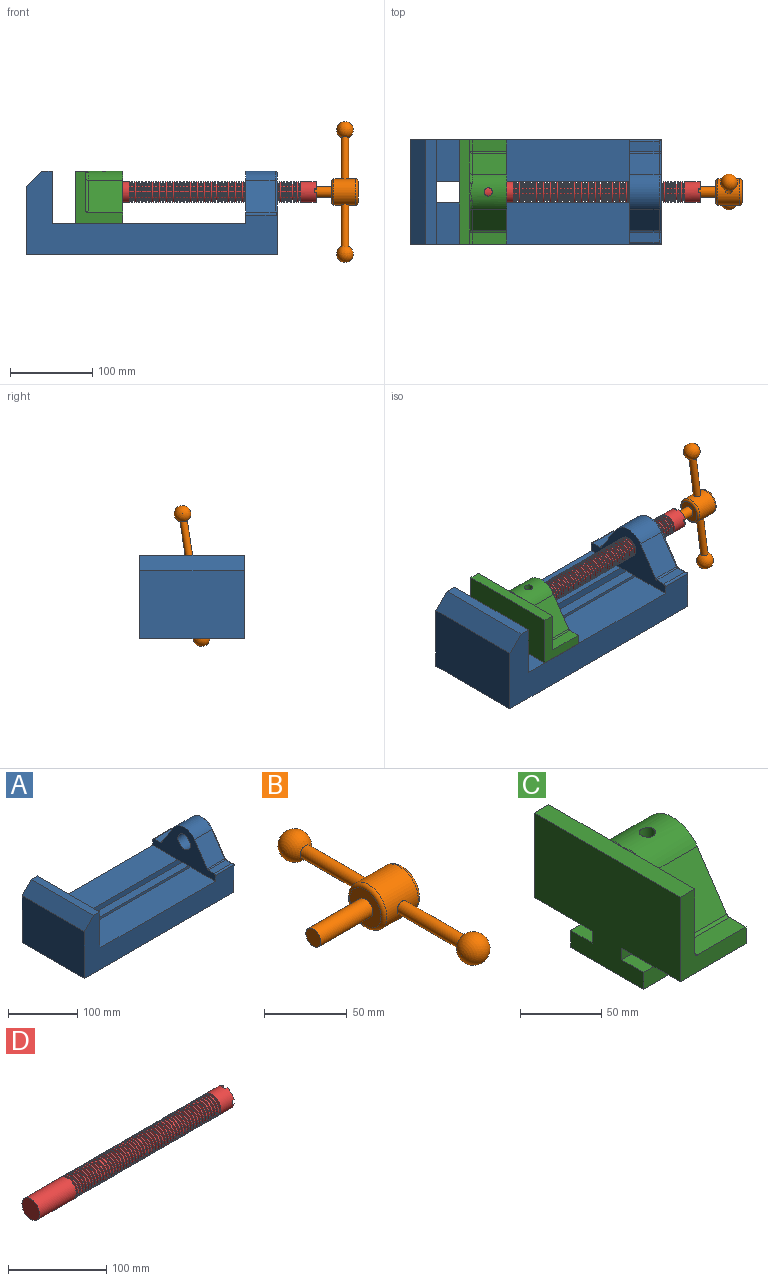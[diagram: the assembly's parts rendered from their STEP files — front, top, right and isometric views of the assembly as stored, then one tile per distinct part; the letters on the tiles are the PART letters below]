
ASSEMBLY  parts=4 mates=4
PART A: 39 faces, bbox 304.8x127x103.7 mm
  f0: plane 234.95x50.8mm, normal (0,0,1), area 11935.5mm2, adj f2,f8,f16,f26
  f1: plane 234.95x50.8mm, normal (0,0,1), area 11935.5mm2, adj f2,f9,f16,f27
  f2: plane 127x101.6mm, normal (1,0,0), area 9516.1mm2, adj f0,f1,f3,f6,f8,f9,f18,f19
  f3: plane 127x12.7mm, normal (0,0,1), area 1612.9mm2, adj f2,f4,f8,f9
  f4: plane 127x19.05mm, normal (-0.71,0,0.71), area 3421.5mm2, adj f3,f5,f8,f9
  f5: plane 127x82.55mm, normal (-1,0,0), area 10483.9mm2, adj f4,f6,f8,f9
  f6: plane 304.8x127mm, normal (0,0,-1), area 31774.1mm2, adj f2,f5,f7,f8,f9,f21,f22
  f7: plane 127x99.06mm, normal (1,0,0), area 7097.5mm2, adj f6,f8,f9,f14,f17,f18,f19,f20
  f8: plane 304.8x101.6mm, normal (0,-1,0), area 13834.6mm2, adj f0,f2,f3,f4,f5,f6,f7,f16
  f9: plane 304.8x101.6mm, normal (0,1,0), area 13834.6mm2, adj f1,f2,f3,f4,f5,f6,f7,f16
  f10: plane 35.56x11.98mm, normal (0,0,1), area 426mm2, adj f16,f28,f29,f30
  f11: plane 38.43x35.56mm, normal (0,0.83,0.56), area 1645.4mm2, adj f12,f16,f29,f32
  f12: cylinder r=25.4mm len=42.19mm, axis (1,0,0), area 1770.2mm2, adj f11,f13,f16,f33
  f13: plane 38.43x35.56mm, normal (0,-0.83,0.56), area 1645.4mm2, adj f12,f16,f34,f35
  f14: cylinder r=12.7mm len=38.1mm, axis (1,0,0), area 3040.2mm2, adj f7,f16
  f15: plane 35.56x11.98mm, normal (0,0,1), area 426mm2, adj f16,f34,f36,f38
  f16: plane 127x63.5mm, normal (-1,0,0), area 4155.5mm2, adj f0,f1,f8,f9,f10,f11,f12,f13
  f17: plane 38.1x25.4mm, normal (0,0,-1), area 967.7mm2, adj f7,f16,f26,f27
  f18: plane 273.05x19.05mm, normal (0,0,-1), area 5201.6mm2, adj f2,f7,f19,f26
  f19: plane 273.05x12.7mm, normal (0,1,0), area 3467.7mm2, adj f2,f7,f18,f20
  f20: plane 273.05x19.05mm, normal (0,0,1), area 5201.6mm2, adj f2,f7,f19,f21
  f21: plane 273.05x16.51mm, normal (0,1,0), area 4508.1mm2, adj f2,f6,f7,f20
  f22: plane 273.05x16.51mm, normal (0,-1,0), area 4508.1mm2, adj f2,f6,f7,f23
  f23: plane 273.05x19.05mm, normal (0,0,1), area 5201.6mm2, adj f2,f7,f22,f24
  f24: plane 273.05x12.7mm, normal (0,-1,0), area 3467.7mm2, adj f2,f7,f23,f25
  f25: plane 273.05x19.05mm, normal (0,0,-1), area 5201.6mm2, adj f2,f7,f24,f27
  f26: plane 273.05x8.89mm, normal (0,1,0), area 2427.4mm2, adj f0,f2,f7,f17,f18
  f27: plane 273.05x8.89mm, normal (0,-1,0), area 2427.4mm2, adj f1,f2,f7,f17,f25
  f28: cylinder r=2.54mm len=38.1mm, axis (1,0,0), area 148.3mm2, adj f9,f10,f16,f30
  f29: cylinder r=2.54mm len=35.56mm, axis (-1,0,0), area 88.5mm2, adj f10,f11,f16,f31
  f30: cylinder r=2.54mm len=14.52mm, axis (0,1,0), area 54.3mm2, adj f7,f10,f28,f31
  f31: torus R=5.08mm, axis (-1,0,0), area 13.5mm2, adj f7,f29,f30,f32
  f32: cylinder r=2.54mm len=39.84mm, axis (0,0.56,-0.83), area 184.6mm2, adj f7,f11,f31,f33
  f33: torus R=22.86mm, axis (-1,0,0), area 191.4mm2, adj f7,f12,f32,f35
  f34: cylinder r=2.54mm len=35.56mm, axis (-1,0,0), area 88.5mm2, adj f13,f15,f16,f37
  f35: cylinder r=2.54mm len=39.84mm, axis (0,0.56,0.83), area 184.6mm2, adj f7,f13,f33,f37
  f36: cylinder r=2.54mm len=38.1mm, axis (-1,0,0), area 148.3mm2, adj f8,f15,f16,f38
  f37: torus R=5.08mm, axis (-1,0,0), area 13.5mm2, adj f7,f34,f35,f38
  f38: cylinder r=2.54mm len=14.52mm, axis (0,1,0), area 54.3mm2, adj f7,f15,f36,f37
PART B: 11 faces, bbox 76.2x172.7x34.4 mm
  f0: sphere r=10.16mm, area 1231.8mm2, adj f1
  f1: cylinder r=4.45mm len=51.82mm, axis (0,1,0), area 1438.5mm2, adj f0,f4
  f2: sphere r=10.16mm, area 1231.8mm2, adj f3
  f3: cylinder r=4.45mm len=51.82mm, axis (0,1,0), area 1438.5mm2, adj f2,f4
  f4: cylinder r=15.88mm len=31.75mm, axis (-1,0,0), area 2534.7mm2, adj f1,f3,f9,f10
  f5: cylinder r=6.35mm len=44.45mm, axis (-1,0,0), area 1773.5mm2, adj f6,f8
  f6: plane 12.7x12.7mm, normal (-1,0,0), area 126.7mm2, adj f5
  f7: plane 26.67x26.67mm, normal (1,0,0), area 558.6mm2, adj f10
  f8: plane 26.67x26.67mm, normal (-1,0,0), area 432mm2, adj f5,f9
  f9: torus R=13.33mm, axis (1,0,0), area 374.8mm2, adj f4,f8
  f10: torus R=13.33mm, axis (1,0,0), area 374.8mm2, adj f4,f7
PART C: 36 faces, bbox 57.2x127x89 mm
  f0: plane 57.15x50.8mm, normal (0,0,-1), area 2903.2mm2, adj f6,f9,f10,f23
  f1: cylinder r=12.7mm len=44.45mm, axis (1,0,0), area 3464.3mm2, adj f6,f15,f16
  f2: plane 41.91x14.52mm, normal (0,0,1), area 608.5mm2, adj f6,f11,f24,f25
  f3: plane 51.86x48.26mm, normal (1,0,0), area 1495.7mm2, adj f8,f10,f31,f33,f35
  f4: plane 51.86x48.26mm, normal (1,0,0), area 1495.7mm2, adj f8,f11,f24,f28,f29
  f5: plane 57.15x50.8mm, normal (0,0,-1), area 2903.2mm2, adj f6,f9,f11,f22
  f6: plane 127x85.09mm, normal (1,0,0), area 5190.6mm2, adj f0,f1,f2,f5,f7,f10,f11,f12
  f7: plane 41.91x14.52mm, normal (0,0,1), area 608.5mm2, adj f6,f10,f30,f31
  f8: plane 127x12.7mm, normal (0,0,1), area 1612.9mm2, adj f3,f4,f9,f10,f11,f26,f34
  f9: plane 127x85.09mm, normal (-1,0,0), area 9096.8mm2, adj f0,f5,f8,f10,f11,f17,f18,f19
  f10: plane 63.5x57.15mm, normal (0,-1,0), area 1372.3mm2, adj f0,f3,f6,f7,f8,f9,f31
  f11: plane 63.5x57.15mm, normal (0,1,0), area 1372.3mm2, adj f2,f4,f5,f6,f8,f9,f24
  f12: plane 41.91x38.43mm, normal (0,-0.83,0.56), area 1939.2mm2, adj f6,f13,f30,f33
  f13: cylinder r=25.4mm len=44.45mm, axis (1,0,0), area 2026.5mm2, adj f6,f12,f14,f16,f26,f28,f34,f35
  f14: plane 41.91x38.43mm, normal (0,0.83,0.56), area 1939.2mm2, adj f6,f13,f25,f29
  f15: plane 25.4x25.4mm, normal (1,0,0), area 506.7mm2, adj f1
  f16: cylinder r=5.08mm len=13.76mm, axis (0,0,1), area 414mm2, adj f1,f13
  f17: plane 57.15x19.05mm, normal (0,0,1), area 1088.7mm2, adj f6,f9,f18,f23
  f18: plane 57.15x12.7mm, normal (0,-1,0), area 725.8mm2, adj f6,f9,f17,f19
  f19: plane 63.5x57.15mm, normal (0,0,-1), area 3629mm2, adj f6,f9,f18,f20
  f20: plane 57.15x12.7mm, normal (0,1,0), area 725.8mm2, adj f6,f9,f19,f21
  f21: plane 57.15x19.05mm, normal (0,0,1), area 1088.7mm2, adj f6,f9,f20,f22
  f22: plane 57.15x8.89mm, normal (0,1,0), area 508.1mm2, adj f5,f6,f9,f21
  f23: plane 57.15x8.89mm, normal (0,-1,0), area 508.1mm2, adj f0,f6,f9,f17
  f24: cylinder r=2.54mm len=14.52mm, axis (0,-1,0), area 57.9mm2, adj f2,f4,f11,f27
  f25: cylinder r=2.54mm len=41.91mm, axis (1,0,0), area 104.3mm2, adj f2,f6,f14,f27
  f26: bspline ~12.24x2.8mm, area 20.9mm2, adj f8,f13,f28
  f27: sphere r=2.54mm, area 6.3mm2, adj f24,f25,f29
  f28: torus R=27.94mm, axis (1,0,0), area 57.8mm2, adj f4,f13,f26,f29
  f29: cylinder r=2.54mm len=39.84mm, axis (0,-0.56,0.83), area 184.6mm2, adj f4,f14,f27,f28
  f30: cylinder r=2.54mm len=41.91mm, axis (1,0,0), area 104.3mm2, adj f6,f7,f12,f32
  f31: cylinder r=2.54mm len=14.52mm, axis (0,-1,0), area 57.9mm2, adj f3,f7,f10,f32
  f32: sphere r=2.54mm, area 6.3mm2, adj f30,f31,f33
  f33: cylinder r=2.54mm len=39.84mm, axis (0,-0.56,-0.83), area 184.6mm2, adj f3,f12,f32,f35
  f34: bspline ~12.24x2.8mm, area 20.9mm2, adj f8,f13,f35
  f35: torus R=27.94mm, axis (1,0,0), area 57.8mm2, adj f3,f13,f33,f34
PART D: 220 faces, bbox 279.4x25.4x25.4 mm
  f0: cylinder r=12.7mm len=25.4mm, axis (-1,0,0), area 1468.2mm2, adj f1,f2,f3,f5,f7,f208,f209,f210
  f1: plane 9.9x9.9mm, normal (1,0,0), area 62.3mm2, adj f0,f4,f213,f216
  f2: plane 9.9x9.9mm, normal (1,0,0), area 62.3mm2, adj f0,f4,f210,f218
  f3: plane 9.9x9.9mm, normal (1,0,0), area 62.3mm2, adj f0,f4,f209,f212
  f4: cylinder r=6.35mm len=25.4mm, axis (1,0,0), area 960.3mm2, adj f1,f2,f3,f5,f6,f208,f209,f210
  f5: plane 9.9x9.9mm, normal (1,0,0), area 62.3mm2, adj f0,f4,f215,f217
  f6: plane 12.7x12.7mm, normal (1,0,0), area 126.7mm2, adj f4
  f7: cone r=12.7mm half-angle=76deg, axis (1,0,0), area 188mm2, adj f0,f9
  f8: cone r=10.16mm half-angle=76deg, axis (-1,0,0), area 188mm2, adj f9,f10
  f9: cylinder r=10.16mm len=20.32mm, axis (1,0,0), area 81.1mm2, adj f7,f8
  f10: cylinder r=12.7mm len=25.4mm, axis (-1,0,0), area 131.7mm2, adj f8,f11
  f11: cone r=12.7mm half-angle=76deg, axis (1,0,0), area 188mm2, adj f10,f13
  f12: cone r=10.16mm half-angle=76deg, axis (-1,0,0), area 188mm2, adj f13,f14
  f13: cylinder r=10.16mm len=20.32mm, axis (1,0,0), area 81.1mm2, adj f11,f12
  f14: cylinder r=12.7mm len=25.4mm, axis (-1,0,0), area 131.7mm2, adj f12,f15
  f15: cone r=12.7mm half-angle=76deg, axis (1,0,0), area 188mm2, adj f14,f17
  f16: cone r=10.16mm half-angle=76deg, axis (-1,0,0), area 188mm2, adj f17,f18
  f17: cylinder r=10.16mm len=20.32mm, axis (1,0,0), area 81.1mm2, adj f15,f16
  f18: cylinder r=12.7mm len=25.4mm, axis (-1,0,0), area 131.7mm2, adj f16,f19
  f19: cone r=12.7mm half-angle=76deg, axis (1,0,0), area 188mm2, adj f18,f21
  f20: cone r=10.16mm half-angle=76deg, axis (-1,0,0), area 188mm2, adj f21,f22
  f21: cylinder r=10.16mm len=20.32mm, axis (1,0,0), area 81.1mm2, adj f19,f20
  f22: cylinder r=12.7mm len=25.4mm, axis (-1,0,0), area 131.7mm2, adj f20,f23
  f23: cone r=12.7mm half-angle=76deg, axis (1,0,0), area 188mm2, adj f22,f25
  f24: cone r=10.16mm half-angle=76deg, axis (-1,0,0), area 188mm2, adj f25,f26
  f25: cylinder r=10.16mm len=20.32mm, axis (1,0,0), area 81.1mm2, adj f23,f24
  f26: cylinder r=12.7mm len=25.4mm, axis (-1,0,0), area 131.7mm2, adj f24,f27
  f27: cone r=12.7mm half-angle=76deg, axis (1,0,0), area 188mm2, adj f26,f29
  f28: cone r=10.16mm half-angle=76deg, axis (-1,0,0), area 188mm2, adj f29,f30
  f29: cylinder r=10.16mm len=20.32mm, axis (1,0,0), area 81.1mm2, adj f27,f28
  f30: cylinder r=12.7mm len=25.4mm, axis (-1,0,0), area 131.7mm2, adj f28,f31
  f31: cone r=12.7mm half-angle=76deg, axis (1,0,0), area 188mm2, adj f30,f33
  f32: cone r=10.16mm half-angle=76deg, axis (-1,0,0), area 188mm2, adj f33,f34
  f33: cylinder r=10.16mm len=20.32mm, axis (1,0,0), area 81.1mm2, adj f31,f32
  f34: cylinder r=12.7mm len=25.4mm, axis (-1,0,0), area 131.7mm2, adj f32,f35
  f35: cone r=12.7mm half-angle=76deg, axis (1,0,0), area 188mm2, adj f34,f37
  f36: cone r=10.16mm half-angle=76deg, axis (-1,0,0), area 188mm2, adj f37,f38
  f37: cylinder r=10.16mm len=20.32mm, axis (1,0,0), area 81.1mm2, adj f35,f36
  f38: cylinder r=12.7mm len=25.4mm, axis (-1,0,0), area 131.7mm2, adj f36,f39
  f39: cone r=12.7mm half-angle=76deg, axis (1,0,0), area 188mm2, adj f38,f41
  f40: cone r=10.16mm half-angle=76deg, axis (-1,0,0), area 188mm2, adj f41,f42
  f41: cylinder r=10.16mm len=20.32mm, axis (1,0,0), area 81.1mm2, adj f39,f40
  f42: cylinder r=12.7mm len=25.4mm, axis (-1,0,0), area 131.7mm2, adj f40,f43
  f43: cone r=12.7mm half-angle=76deg, axis (1,0,0), area 188mm2, adj f42,f45
  f44: cone r=10.16mm half-angle=76deg, axis (-1,0,0), area 188mm2, adj f45,f46
  f45: cylinder r=10.16mm len=20.32mm, axis (1,0,0), area 81.1mm2, adj f43,f44
  f46: cylinder r=12.7mm len=25.4mm, axis (-1,0,0), area 131.7mm2, adj f44,f47
  f47: cone r=12.7mm half-angle=76deg, axis (1,0,0), area 188mm2, adj f46,f49
  f48: cone r=10.16mm half-angle=76deg, axis (-1,0,0), area 188mm2, adj f49,f50
  f49: cylinder r=10.16mm len=20.32mm, axis (1,0,0), area 81.1mm2, adj f47,f48
  f50: cylinder r=12.7mm len=25.4mm, axis (-1,0,0), area 131.7mm2, adj f48,f51
  f51: cone r=12.7mm half-angle=76deg, axis (1,0,0), area 188mm2, adj f50,f53
  f52: cone r=10.16mm half-angle=76deg, axis (-1,0,0), area 188mm2, adj f53,f54
  f53: cylinder r=10.16mm len=20.32mm, axis (1,0,0), area 81.1mm2, adj f51,f52
  f54: cylinder r=12.7mm len=25.4mm, axis (-1,0,0), area 131.7mm2, adj f52,f55
  f55: cone r=12.7mm half-angle=76deg, axis (1,0,0), area 188mm2, adj f54,f57
  f56: cone r=10.16mm half-angle=76deg, axis (-1,0,0), area 188mm2, adj f57,f58
  f57: cylinder r=10.16mm len=20.32mm, axis (1,0,0), area 81.1mm2, adj f55,f56
  f58: cylinder r=12.7mm len=25.4mm, axis (-1,0,0), area 131.7mm2, adj f56,f59
  f59: cone r=12.7mm half-angle=76deg, axis (1,0,0), area 188mm2, adj f58,f61
  f60: cone r=10.16mm half-angle=76deg, axis (-1,0,0), area 188mm2, adj f61,f62
  f61: cylinder r=10.16mm len=20.32mm, axis (1,0,0), area 81.1mm2, adj f59,f60
  f62: cylinder r=12.7mm len=25.4mm, axis (-1,0,0), area 131.7mm2, adj f60,f63
  f63: cone r=12.7mm half-angle=76deg, axis (1,0,0), area 188mm2, adj f62,f65
  f64: cone r=10.16mm half-angle=76deg, axis (-1,0,0), area 188mm2, adj f65,f66
  f65: cylinder r=10.16mm len=20.32mm, axis (1,0,0), area 81.1mm2, adj f63,f64
  f66: cylinder r=12.7mm len=25.4mm, axis (-1,0,0), area 131.7mm2, adj f64,f67
  f67: cone r=12.7mm half-angle=76deg, axis (1,0,0), area 188mm2, adj f66,f69
  f68: cone r=10.16mm half-angle=76deg, axis (-1,0,0), area 188mm2, adj f69,f70
  f69: cylinder r=10.16mm len=20.32mm, axis (1,0,0), area 81.1mm2, adj f67,f68
  f70: cylinder r=12.7mm len=25.4mm, axis (-1,0,0), area 131.7mm2, adj f68,f71
  f71: cone r=12.7mm half-angle=76deg, axis (1,0,0), area 188mm2, adj f70,f73
  f72: cone r=10.16mm half-angle=76deg, axis (-1,0,0), area 188mm2, adj f73,f74
  f73: cylinder r=10.16mm len=20.32mm, axis (1,0,0), area 81.1mm2, adj f71,f72
  f74: cylinder r=12.7mm len=25.4mm, axis (-1,0,0), area 131.7mm2, adj f72,f75
  f75: cone r=12.7mm half-angle=76deg, axis (1,0,0), area 188mm2, adj f74,f77
  f76: cone r=10.16mm half-angle=76deg, axis (-1,0,0), area 188mm2, adj f77,f78
  f77: cylinder r=10.16mm len=20.32mm, axis (1,0,0), area 81.1mm2, adj f75,f76
  f78: cylinder r=12.7mm len=25.4mm, axis (-1,0,0), area 131.7mm2, adj f76,f79
  f79: cone r=12.7mm half-angle=76deg, axis (1,0,0), area 188mm2, adj f78,f81
  f80: cone r=10.16mm half-angle=76deg, axis (-1,0,0), area 188mm2, adj f81,f82
  f81: cylinder r=10.16mm len=20.32mm, axis (1,0,0), area 81.1mm2, adj f79,f80
  f82: cylinder r=12.7mm len=25.4mm, axis (-1,0,0), area 131.7mm2, adj f80,f83
  f83: cone r=12.7mm half-angle=76deg, axis (1,0,0), area 188mm2, adj f82,f85
  f84: cone r=10.16mm half-angle=76deg, axis (-1,0,0), area 188mm2, adj f85,f86
  f85: cylinder r=10.16mm len=20.32mm, axis (1,0,0), area 81.1mm2, adj f83,f84
  f86: cylinder r=12.7mm len=25.4mm, axis (-1,0,0), area 131.7mm2, adj f84,f87
  f87: cone r=12.7mm half-angle=76deg, axis (1,0,0), area 188mm2, adj f86,f89
  f88: cone r=10.16mm half-angle=76deg, axis (-1,0,0), area 188mm2, adj f89,f90
  f89: cylinder r=10.16mm len=20.32mm, axis (1,0,0), area 81.1mm2, adj f87,f88
  f90: cylinder r=12.7mm len=25.4mm, axis (-1,0,0), area 131.7mm2, adj f88,f91
  f91: cone r=12.7mm half-angle=76deg, axis (1,0,0), area 188mm2, adj f90,f93
  f92: cone r=10.16mm half-angle=76deg, axis (-1,0,0), area 188mm2, adj f93,f94
  f93: cylinder r=10.16mm len=20.32mm, axis (1,0,0), area 81.1mm2, adj f91,f92
  f94: cylinder r=12.7mm len=25.4mm, axis (-1,0,0), area 131.7mm2, adj f92,f95
  f95: cone r=12.7mm half-angle=76deg, axis (1,0,0), area 188mm2, adj f94,f97
  f96: cone r=10.16mm half-angle=76deg, axis (-1,0,0), area 188mm2, adj f97,f98
  f97: cylinder r=10.16mm len=20.32mm, axis (1,0,0), area 81.1mm2, adj f95,f96
  f98: cylinder r=12.7mm len=25.4mm, axis (-1,0,0), area 131.7mm2, adj f96,f99
  f99: cone r=12.7mm half-angle=76deg, axis (1,0,0), area 188mm2, adj f98,f101
  f100: cone r=10.16mm half-angle=76deg, axis (-1,0,0), area 188mm2, adj f101,f102
  f101: cylinder r=10.16mm len=20.32mm, axis (1,0,0), area 81.1mm2, adj f99,f100
  f102: cylinder r=12.7mm len=25.4mm, axis (-1,0,0), area 131.7mm2, adj f100,f103
  f103: cone r=12.7mm half-angle=76deg, axis (1,0,0), area 188mm2, adj f102,f105
  f104: cone r=10.16mm half-angle=76deg, axis (-1,0,0), area 188mm2, adj f105,f106
  f105: cylinder r=10.16mm len=20.32mm, axis (1,0,0), area 81.1mm2, adj f103,f104
  f106: cylinder r=12.7mm len=25.4mm, axis (-1,0,0), area 131.7mm2, adj f104,f107
  f107: cone r=12.7mm half-angle=76deg, axis (1,0,0), area 188mm2, adj f106,f109
  f108: cone r=10.16mm half-angle=76deg, axis (-1,0,0), area 188mm2, adj f109,f110
  f109: cylinder r=10.16mm len=20.32mm, axis (1,0,0), area 81.1mm2, adj f107,f108
  f110: cylinder r=12.7mm len=25.4mm, axis (-1,0,0), area 131.7mm2, adj f108,f111
  f111: cone r=12.7mm half-angle=76deg, axis (1,0,0), area 188mm2, adj f110,f113
  f112: cone r=10.16mm half-angle=76deg, axis (-1,0,0), area 188mm2, adj f113,f114
  f113: cylinder r=10.16mm len=20.32mm, axis (1,0,0), area 81.1mm2, adj f111,f112
  f114: cylinder r=12.7mm len=25.4mm, axis (-1,0,0), area 131.7mm2, adj f112,f115
  f115: cone r=12.7mm half-angle=76deg, axis (1,0,0), area 188mm2, adj f114,f117
  f116: cone r=10.16mm half-angle=76deg, axis (-1,0,0), area 188mm2, adj f117,f118
  f117: cylinder r=10.16mm len=20.32mm, axis (1,0,0), area 81.1mm2, adj f115,f116
  f118: cylinder r=12.7mm len=25.4mm, axis (-1,0,0), area 131.7mm2, adj f116,f119
  f119: cone r=12.7mm half-angle=76deg, axis (1,0,0), area 188mm2, adj f118,f121
  f120: cone r=10.16mm half-angle=76deg, axis (-1,0,0), area 188mm2, adj f121,f122
  f121: cylinder r=10.16mm len=20.32mm, axis (1,0,0), area 81.1mm2, adj f119,f120
  f122: cylinder r=12.7mm len=25.4mm, axis (-1,0,0), area 131.7mm2, adj f120,f123
  f123: cone r=12.7mm half-angle=76deg, axis (1,0,0), area 188mm2, adj f122,f125
  f124: cone r=10.16mm half-angle=76deg, axis (-1,0,0), area 188mm2, adj f125,f126
  f125: cylinder r=10.16mm len=20.32mm, axis (1,0,0), area 81.1mm2, adj f123,f124
  f126: cylinder r=12.7mm len=25.4mm, axis (-1,0,0), area 131.7mm2, adj f124,f127
  f127: cone r=12.7mm half-angle=76deg, axis (1,0,0), area 188mm2, adj f126,f129
  f128: cone r=10.16mm half-angle=76deg, axis (-1,0,0), area 188mm2, adj f129,f130
  f129: cylinder r=10.16mm len=20.32mm, axis (1,0,0), area 81.1mm2, adj f127,f128
  f130: cylinder r=12.7mm len=25.4mm, axis (-1,0,0), area 131.7mm2, adj f128,f131
  f131: cone r=12.7mm half-angle=76deg, axis (1,0,0), area 188mm2, adj f130,f133
  f132: cone r=10.16mm half-angle=76deg, axis (-1,0,0), area 188mm2, adj f133,f134
  f133: cylinder r=10.16mm len=20.32mm, axis (1,0,0), area 81.1mm2, adj f131,f132
  f134: cylinder r=12.7mm len=25.4mm, axis (-1,0,0), area 131.7mm2, adj f132,f135
  f135: cone r=12.7mm half-angle=76deg, axis (1,0,0), area 188mm2, adj f134,f137
  f136: cone r=10.16mm half-angle=76deg, axis (-1,0,0), area 188mm2, adj f137,f138
  f137: cylinder r=10.16mm len=20.32mm, axis (1,0,0), area 81.1mm2, adj f135,f136
  f138: cylinder r=12.7mm len=25.4mm, axis (-1,0,0), area 131.7mm2, adj f136,f139
  f139: cone r=12.7mm half-angle=76deg, axis (1,0,0), area 188mm2, adj f138,f141
  f140: cone r=10.16mm half-angle=76deg, axis (-1,0,0), area 188mm2, adj f141,f142
  f141: cylinder r=10.16mm len=20.32mm, axis (1,0,0), area 81.1mm2, adj f139,f140
  f142: cylinder r=12.7mm len=25.4mm, axis (-1,0,0), area 131.7mm2, adj f140,f143
  f143: cone r=12.7mm half-angle=76deg, axis (1,0,0), area 188mm2, adj f142,f145
  f144: cone r=10.16mm half-angle=76deg, axis (-1,0,0), area 188mm2, adj f145,f146
  f145: cylinder r=10.16mm len=20.32mm, axis (1,0,0), area 81.1mm2, adj f143,f144
  f146: cylinder r=12.7mm len=25.4mm, axis (-1,0,0), area 131.7mm2, adj f144,f147
  f147: cone r=12.7mm half-angle=76deg, axis (1,0,0), area 188mm2, adj f146,f149
  f148: cone r=10.16mm half-angle=76deg, axis (-1,0,0), area 188mm2, adj f149,f150
  f149: cylinder r=10.16mm len=20.32mm, axis (1,0,0), area 81.1mm2, adj f147,f148
  f150: cylinder r=12.7mm len=25.4mm, axis (-1,0,0), area 131.7mm2, adj f148,f151
  f151: cone r=12.7mm half-angle=76deg, axis (1,0,0), area 188mm2, adj f150,f153
  f152: cone r=10.16mm half-angle=76deg, axis (-1,0,0), area 188mm2, adj f153,f154
  f153: cylinder r=10.16mm len=20.32mm, axis (1,0,0), area 81.1mm2, adj f151,f152
  f154: cylinder r=12.7mm len=25.4mm, axis (-1,0,0), area 131.7mm2, adj f152,f155
  f155: cone r=12.7mm half-angle=76deg, axis (1,0,0), area 188mm2, adj f154,f157
  f156: cone r=10.16mm half-angle=76deg, axis (-1,0,0), area 188mm2, adj f157,f158
  f157: cylinder r=10.16mm len=20.32mm, axis (1,0,0), area 81.1mm2, adj f155,f156
  f158: cylinder r=12.7mm len=25.4mm, axis (-1,0,0), area 131.7mm2, adj f156,f159
  f159: cone r=12.7mm half-angle=76deg, axis (1,0,0), area 188mm2, adj f158,f161
  f160: cone r=10.16mm half-angle=76deg, axis (-1,0,0), area 188mm2, adj f161,f162
  f161: cylinder r=10.16mm len=20.32mm, axis (1,0,0), area 81.1mm2, adj f159,f160
  f162: cylinder r=12.7mm len=25.4mm, axis (-1,0,0), area 131.7mm2, adj f160,f163
  f163: cone r=12.7mm half-angle=76deg, axis (1,0,0), area 188mm2, adj f162,f165
  f164: cone r=10.16mm half-angle=76deg, axis (-1,0,0), area 188mm2, adj f165,f166
  f165: cylinder r=10.16mm len=20.32mm, axis (1,0,0), area 81.1mm2, adj f163,f164
  f166: cylinder r=12.7mm len=25.4mm, axis (-1,0,0), area 131.7mm2, adj f164,f167
  f167: cone r=12.7mm half-angle=76deg, axis (1,0,0), area 188mm2, adj f166,f169
  f168: cone r=10.16mm half-angle=76deg, axis (-1,0,0), area 188mm2, adj f169,f170
  f169: cylinder r=10.16mm len=20.32mm, axis (1,0,0), area 81.1mm2, adj f167,f168
  f170: cylinder r=12.7mm len=25.4mm, axis (-1,0,0), area 131.7mm2, adj f168,f171
  f171: cone r=12.7mm half-angle=76deg, axis (1,0,0), area 188mm2, adj f170,f173
  f172: cone r=10.16mm half-angle=76deg, axis (-1,0,0), area 188mm2, adj f173,f174
  f173: cylinder r=10.16mm len=20.32mm, axis (1,0,0), area 81.1mm2, adj f171,f172
  f174: cylinder r=12.7mm len=25.4mm, axis (-1,0,0), area 131.7mm2, adj f172,f175
  f175: cone r=12.7mm half-angle=76deg, axis (1,0,0), area 188mm2, adj f174,f177
  f176: cone r=10.16mm half-angle=76deg, axis (-1,0,0), area 188mm2, adj f177,f178
  f177: cylinder r=10.16mm len=20.32mm, axis (1,0,0), area 81.1mm2, adj f175,f176
  f178: cylinder r=12.7mm len=25.4mm, axis (-1,0,0), area 131.7mm2, adj f176,f179
  f179: cone r=12.7mm half-angle=76deg, axis (1,0,0), area 188mm2, adj f178,f181
  f180: cone r=10.16mm half-angle=76deg, axis (-1,0,0), area 188mm2, adj f181,f182
  f181: cylinder r=10.16mm len=20.32mm, axis (1,0,0), area 81.1mm2, adj f179,f180
  f182: cylinder r=12.7mm len=25.4mm, axis (-1,0,0), area 131.7mm2, adj f180,f183
  f183: cone r=12.7mm half-angle=76deg, axis (1,0,0), area 188mm2, adj f182,f185
  f184: cone r=10.16mm half-angle=76deg, axis (-1,0,0), area 188mm2, adj f185,f186
  f185: cylinder r=10.16mm len=20.32mm, axis (1,0,0), area 81.1mm2, adj f183,f184
  f186: cylinder r=12.7mm len=25.4mm, axis (-1,0,0), area 131.7mm2, adj f184,f187
  f187: cone r=12.7mm half-angle=76deg, axis (1,0,0), area 188mm2, adj f186,f189
  f188: cone r=10.16mm half-angle=76deg, axis (-1,0,0), area 188mm2, adj f189,f190
  f189: cylinder r=10.16mm len=20.32mm, axis (1,0,0), area 81.1mm2, adj f187,f188
  f190: cylinder r=12.7mm len=25.4mm, axis (-1,0,0), area 131.7mm2, adj f188,f191
  f191: cone r=12.7mm half-angle=76deg, axis (1,0,0), area 188mm2, adj f190,f193
  f192: cone r=10.16mm half-angle=76deg, axis (-1,0,0), area 188mm2, adj f193,f194
  f193: cylinder r=10.16mm len=20.32mm, axis (1,0,0), area 81.1mm2, adj f191,f192
  f194: cylinder r=12.7mm len=25.4mm, axis (-1,0,0), area 131.7mm2, adj f192,f195
  f195: cone r=12.7mm half-angle=76deg, axis (1,0,0), area 188mm2, adj f194,f197
  f196: cone r=10.16mm half-angle=76deg, axis (-1,0,0), area 188mm2, adj f197,f198
  f197: cylinder r=10.16mm len=20.32mm, axis (1,0,0), area 81.1mm2, adj f195,f196
  f198: cylinder r=12.7mm len=25.4mm, axis (-1,0,0), area 131.7mm2, adj f196,f199
  f199: cone r=12.7mm half-angle=76deg, axis (1,0,0), area 188mm2, adj f198,f201
  f200: cone r=10.16mm half-angle=76deg, axis (-1,0,0), area 188mm2, adj f201,f202
  f201: cylinder r=10.16mm len=20.32mm, axis (1,0,0), area 81.1mm2, adj f199,f200
  f202: cylinder r=12.7mm len=25.4mm, axis (-1,0,0), area 131.7mm2, adj f200,f203
  f203: cone r=12.7mm half-angle=76deg, axis (1,0,0), area 188mm2, adj f202,f205
  f204: cone r=10.16mm half-angle=76deg, axis (-1,0,0), area 188mm2, adj f205,f207
  f205: cylinder r=10.16mm len=20.32mm, axis (1,0,0), area 81.1mm2, adj f203,f204
  f206: plane 25.4x25.4mm, normal (-1,0,0), area 506.7mm2, adj f207
  f207: cylinder r=12.7mm len=52.45mm, axis (-1,0,0), area 4185.4mm2, adj f204,f206
  f208: plane 6.88x5.08mm, normal (1,0,0), area 32.7mm2, adj f0,f4,f209,f210
  f209: plane 6.62x2.54mm, normal (0,-1,0), area 16.8mm2, adj f0,f3,f4,f208
  f210: plane 6.62x2.54mm, normal (0,1,0), area 16.8mm2, adj f0,f2,f4,f208
  f211: plane 6.88x5.08mm, normal (1,0,0), area 32.7mm2, adj f0,f4,f212,f213
  f212: plane 6.62x2.54mm, normal (0,0,1), area 16.8mm2, adj f0,f3,f4,f211
  f213: plane 6.62x2.54mm, normal (0,0,-1), area 16.8mm2, adj f0,f1,f4,f211
  f214: plane 6.88x5.08mm, normal (1,0,0), area 32.7mm2, adj f0,f4,f215,f216
  f215: plane 6.62x2.54mm, normal (0,1,0), area 16.8mm2, adj f0,f4,f5,f214
  f216: plane 6.62x2.54mm, normal (0,-1,0), area 16.8mm2, adj f0,f1,f4,f214
  f217: plane 6.62x2.54mm, normal (0,0,-1), area 16.8mm2, adj f0,f4,f5,f219
  f218: plane 6.62x2.54mm, normal (0,0,1), area 16.8mm2, adj f0,f2,f4,f219
  f219: plane 6.88x5.08mm, normal (1,0,0), area 32.7mm2, adj f0,f4,f217,f218
PLACE A t=(10.81,-41.71,9.26)mm fixed
PLACE B rot(axis=(-1,0,0),98.6deg) t=(39.08,-117.04,96.92)mm
PLACE C t=(39.08,-41.71,9.26)mm
PLACE D rot(axis=(1,0,0),171.4deg) t=(39.08,-30.25,160.79)mm
MATE cylindrical A.f12 <-> D.f4  axis (1,0,0) through (10.81,-41.71,85.46)mm
MATE fastened D.f4 <-> B.f5  axis (1,0,0) through (32.73,-41.71,85.46)mm
MATE slider C.f6 <-> A.f2  axis (1,0,0) through (-176.82,-105.21,47.36)mm
MATE revolute D.f7 <-> C.f28  axis (-1,0,0) through (-221.27,-41.71,85.46)mm
